# Revit family: Thorn AVENUE D2
name_source: partatom
category: Lighting Fixtures
revit_build: Autodesk Revit 2016 (Build: 20150220_1215(x64)
units: mm (PartAtom-declared; Revit-internal decimal feet)

## family parameters
Always vertical = Yes
Cut with Voids When Loaded = No
Light Source = Yes
OmniClass Number = 23.80.70.11
OmniClass Title = Luminaries for Internal Lighting
Part Type = Normal
Room Calculation Point = No
Round Connector Dimension = Use Diameter
Shared = No
Work Plane-Based = No

## types (2) — shared parameters
Apparent Load = 21 VA
Assembly Code = D5020210
Body = Thorn_Metal_Dark_Grey
Color Filter = 16777215
Cover = Thorn_Glass_Self_llumination_Transparent
Description = LED Amenity lighting lantern
Dimming Lamp Color Temperature Shift = <None>
Emit Shape Visible in Rendering = No
Emit from Circle Diameter = 201 mm  [stored 0.659449 ft]
Height = 732 mm
Lamp = LED
Length = 596 mm  [stored 1.95538 ft]
Manufacturer = Thorn Lighting
Tilt Angle = -90.00°
Voltage = 230 V
Width = 596 mm  [stored 1.95538 ft]

## per-type parameters (varying)
| type | Model | Photometric Web File | URL |
| Avenue D2 R/S | 96261383 | TLLA_AVD18L35RS3KG33_DC.IES | www.thornlighting.com/96261383 |
| Avenue D2 WST | 96261401 | TLLA_AVD18L35WST4KG33_DC.IES | www.thornlighting.com/96261401 |

note: [stored X ft] marks values corroborated as IEEE doubles in the binary element streams (Revit-internal decimal feet)

## geometry (parser evidence)
native form markers: Blend x8, Sweep x2
no freeform markers — native parametric forms only
